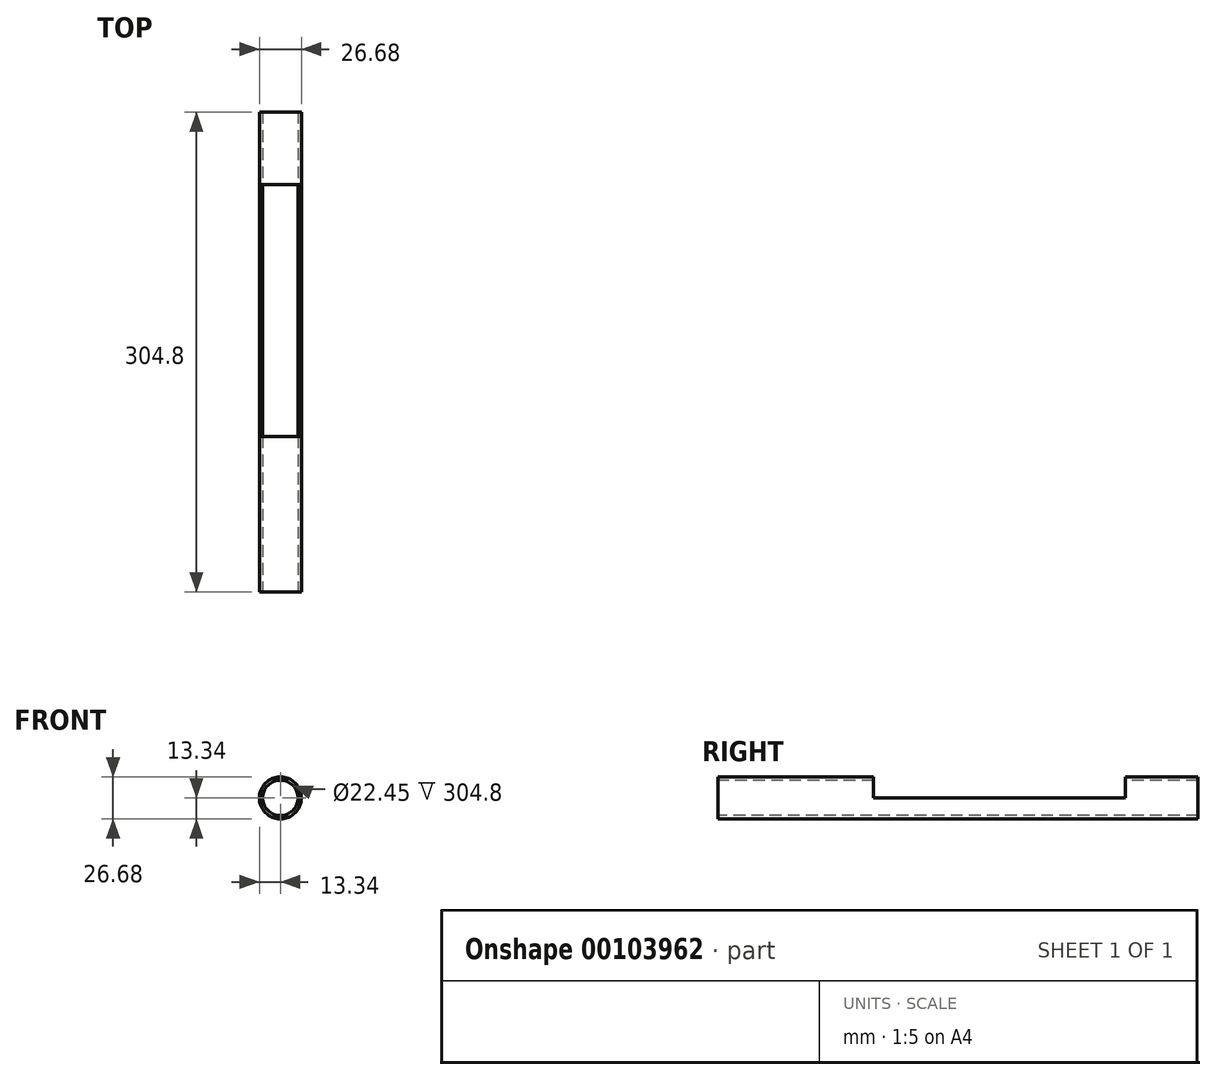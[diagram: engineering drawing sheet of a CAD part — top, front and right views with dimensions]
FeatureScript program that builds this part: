
annotation { "Feature Type Name" : "Feature", "Feature Type Description" : "" }
export const myFeature = defineFeature(function(context is Context, id is Id, definition is map)
    precondition{}
    {
        {
            var Q0;
            Q0=qCreatedBy(makeId("Front.planeOp"),FACE);
            var sketch = newSketch(context, id + "F0", { "sketchPlane" : qUnion([Q0])});
            skCircle(sketch, "E0", {"center": v(0, 0) * mm, "radius": 13.34 * mm});
            skSolve(sketch);
        }
        {
            var Q0;
            Q0 = qSketchRegion(id + "F0", true);
            extrude(context, id + "F1", {"entities" : qUnion([Q0]), "depth" : 304.8 * mm});
        }
        {
            var Q0;
            Q0=makeQuery(id+"F1.opExtrude","CAP_FACE",FACE,{"disambiguationData":[OSD([sQuery(id+"F0.wireOp",EDGE,"E0")])],"isStart":false});
            var sketch = newSketch(context, id + "F2", { "sketchPlane" : qUnion([Q0])});
            skCircle(sketch, "E1", {"center": v(0, 0) * mm, "radius": 11.23 * mm});
            skSolve(sketch);
        }
        {
            var Q0;
            Q0 = qSketchRegion(id + "F2", true);
            extrude(context, id + "F3", {"entities" : qUnion([Q0]), "operationType" : NewBodyOperationType.REMOVE, "endBound" : BoundingType.THROUGH_ALL, "oppositeDirection" : true, "depth" : 25 * mm});
        }
        {
            var Q0;
            Q0=qCreatedBy(makeId("Top.planeOp"),FACE);
            cPlane(context, id + "F4", {"entities" : qUnion([Q0]), "cplaneType" : CPlaneType.OFFSET, "offset" : 13.34 * mm, "width" : 150 * mm, "height" : 150 * mm});
        }
        {
            var Q0;
            Q0=qCreatedBy(id+"F4.planeOp",FACE);
            var sketch = newSketch(context, id + "F5", { "sketchPlane" : qUnion([Q0])});
            skLineSegment(sketch, "E2.bottom", {"start": v(-13.33, -46) * mm, "end": v(13.33, -46) * mm});
            skLineSegment(sketch, "E2.top", {"start": v(-13.33, -206) * mm, "end": v(13.34, -206) * mm});
            skLineSegment(sketch, "E2.left", {"start": v(-13.33, -46) * mm, "end": v(-13.33, -206) * mm});
            skLineSegment(sketch, "E2.right", {"start": v(13.34, -46) * mm, "end": v(13.34, -206) * mm});
            skPoint(sketch, "E3", {"position": v(0, -46) * mm});
            skSolve(sketch);
        }
        {
            var Q0;
            Q0 = qSketchRegion(id + "F5", true);
            extrude(context, id + "F6", {"entities" : qUnion([Q0]), "operationType" : NewBodyOperationType.REMOVE, "oppositeDirection" : true, "depth" : 13.34 * mm});
        }
    });
